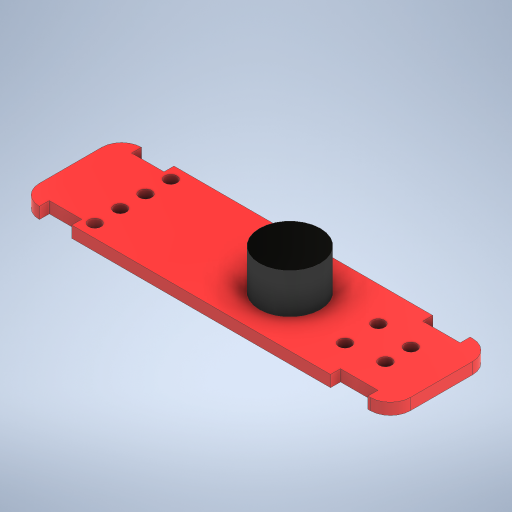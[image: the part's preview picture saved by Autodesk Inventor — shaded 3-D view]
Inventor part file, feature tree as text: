
AUTODESK INVENTOR PART (.ipt)
format: ipt  version: 2023 (Build 270158030, 158C)  size: 317,952 bytes
history: native  units: mm
features: extrude x2, sketch x2
ambient origin geometry x8: Origin, YZ Plane, XZ Plane, XY Plane, X Axis, Y Axis, Z Axis, Center Point
bodies: Solid1 (feature_tree)
feature tree (4):
  extrude  "Extrusion1"  Depth=10.25mm
  extrude  "Extrusion2"  Depth=4.0mm
  sketch  "Sketch1"  dims[d0=37.2mm d1=10.25mm]
  sketch  "Sketch2"  dims[d2=4.35mm d3=8.0mm d4=3.85mm d5=3.85mm d6=2.545mm d7=2.54mm d8=2.54mm d9=2.54mm d10=2.0mm d11=6.25mm d12=3.45mm d13=3.45mm d14=1.25mm d15=1.315mm d16=1.315mm d17=2.25mm d18=6.0mm d19=1.0mm d20=1.0mm d22=5.25mm d23=2.0mm d24=10.25mm d25=1.0mm d26=3.75mm d27=1.0mm d28=2.0mm d29=2.0mm d30=1.315mm d31=1.315mm d32=3.45mm d33=3.45mm d34=3.85mm d35=1.25mm d36=3.855mm d37=1.15mm d38=0.0mm d39=6.1mm d40=15.2mm d41=5.125mm d42=5.125mm d43=4.0mm d44=0.0mm]
